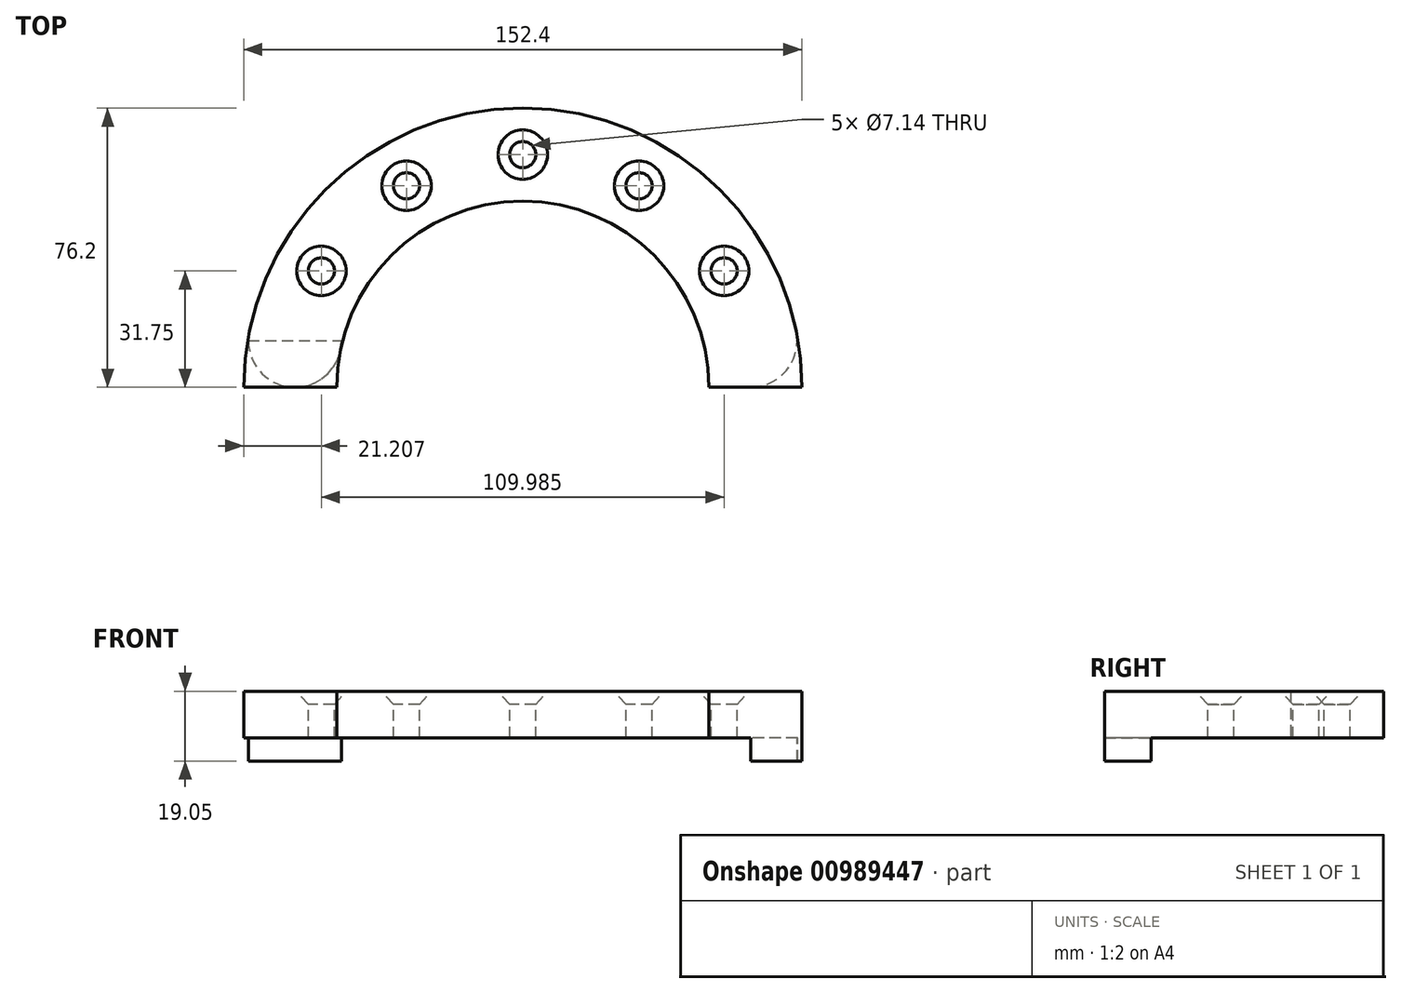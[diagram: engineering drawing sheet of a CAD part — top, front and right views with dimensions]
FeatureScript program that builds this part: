
annotation { "Feature Type Name" : "Feature", "Feature Type Description" : "" }
export const myFeature = defineFeature(function(context is Context, id is Id, definition is map)
    precondition{}
    {
        {
            var Q0;
            Q0=qCreatedBy(makeId("Top.planeOp"),FACE);
            var sketch = newSketch(context, id + "F0", { "sketchPlane" : qUnion([Q0])});
            skArc(sketch, "E0", {"start": v(-50.8, 0) * mm, "mid": v(0, 50.8) * mm, "end": v(50.8, 0) * mm});
            skArc(sketch, "E1", {"start": v(-76.2, 0) * mm, "mid": v(0, 76.2) * mm, "end": v(76.2, 0) * mm});
            skLineSegment(sketch, "E2", {"start": v(-76.2, 0) * mm, "end": v(-50.8, 0) * mm});
            skLineSegment(sketch, "E3", {"start": v(50.8, 0) * mm, "end": v(76.2, 0) * mm});
            skSolve(sketch);
        }
        {
            var Q0;
            Q0 = qSketchRegion(id + "F0", true);
            extrude(context, id + "F1", {"entities" : qUnion([Q0]), "depth" : 12.7 * mm, "offsetDistance" : 25.4 * mm});
        }
        {
            var Q0;
            Q0=makeQuery(id+"F1.opExtrude","CAP_FACE",FACE,{"disambiguationData":[OSD([sQuery(id+"F0.wireOp",EDGE,"E0"),sQuery(id+"F0.wireOp",EDGE,"E1"),sQuery(id+"F0.wireOp",EDGE,"E2"),sQuery(id+"F0.wireOp",EDGE,"E3")])],"isStart":true});
            var sketch = newSketch(context, id + "F2", { "sketchPlane" : qUnion([Q0])});
            skArc(sketch, "E4", {"start": v(-49.52, -12.7) * mm, "mid": v(-62.22, 0) * mm, "end": v(-74.92, -12.7) * mm});
            skLineSegment(sketch, "E5", {"start": v(-75.13, -12.7) * mm, "end": v(-49.52, -12.7) * mm});
            skPoint(sketch, "E6.MirrorCS.end.orphan", {"position": v(-74.92, -12.7) * mm});
            skPoint(sketch, "E6.MirrorCS.start.orphan", {"position": v(-49.52, -12.7) * mm});
            skLineSegment(sketch, "E7", {"start": v(0, 0) * mm, "end": v(0, 11.59) * mm, "construction": true});
            skArc(sketch, "E8.MirrorCS", {"start": v(49.52, -12.7) * mm, "mid": v(62.22, 0) * mm, "end": v(74.92, -12.7) * mm});
            skLineSegment(sketch, "E9.MirrorCS", {"start": v(75.13, -12.7) * mm, "end": v(49.52, -12.7) * mm});
            skPoint(sketch, "E10.MirrorP", {"position": v(49.52, -12.7) * mm});
            skPoint(sketch, "E11.MirrorP", {"position": v(74.92, -12.7) * mm});
            skSolve(sketch);
        }
        {
            var Q0;
            {var subQ0=sQuery(id+"F2.wireOp",EDGE,"E8.MirrorCS");var subQ1=sQuery(id+"F2.wireOp",EDGE,"E9.MirrorCS");var subQ2=makeQuery(id+"F2.imprint","INTERSECT",VERTEX,{"disambiguationData":[OD(0.0)],"derivedFrom":[subQ1,subQ0]});Q0=makeQuery(id+"F2.imprint","IMPRINT",FACE,{"disambiguationData":[TD([[makeQuery(id+"F2.imprint","IMPRINT",EDGE,{"disambiguationData":[TD([[subQ2,1.0]])],"derivedFrom":subQ1}),-1.0]])]});}
            var Q1;
            {var subQ0=sQuery(id+"F2.wireOp",EDGE,"E5");var subQ1=sQuery(id+"F2.wireOp",EDGE,"E4");var subQ2=makeQuery(id+"F2.imprint","INTERSECT",VERTEX,{"disambiguationData":[OD(0.0)],"derivedFrom":[subQ1,subQ0]});Q1=makeQuery(id+"F2.imprint","IMPRINT",FACE,{"disambiguationData":[TD([[makeQuery(id+"F2.imprint","IMPRINT",EDGE,{"disambiguationData":[TD([[subQ2,-1.0]])],"derivedFrom":subQ1}),1.0]])]});}
            extrude(context, id + "F3", {"entities" : qUnion([Q0, Q1]), "operationType" : NewBodyOperationType.ADD, "depth" : 6.35 * mm, "offsetDistance" : 25.4 * mm});
        }
        {
            var Q0;
            Q0=makeQuery(id+"F1.opExtrude","CAP_FACE",FACE,{"disambiguationData":[OSD([sQuery(id+"F0.wireOp",EDGE,"E0"),sQuery(id+"F0.wireOp",EDGE,"E1"),sQuery(id+"F0.wireOp",EDGE,"E2"),sQuery(id+"F0.wireOp",EDGE,"E3")])],"isStart":false});
            var sketch = newSketch(context, id + "F4", { "sketchPlane" : qUnion([Q0])});
            skArc(sketch, "E12", {"start": v(-63.5, 0) * mm, "mid": v(0, 63.5) * mm, "end": v(63.5, 0) * mm, "construction": true});
            skPoint(sketch, "E13", {"position": v(-63.5, 0) * mm});
            skPoint(sketch, "E14.1.0", {"position": v(-55, 31.75) * mm});
            skPoint(sketch, "E14.2.0", {"position": v(-31.75, 55) * mm});
            skPoint(sketch, "E14.3.0", {"position": v(0, 63.5) * mm});
            skPoint(sketch, "E14.4.0", {"position": v(31.75, 55) * mm});
            skPoint(sketch, "E14.5.0", {"position": v(55, 31.75) * mm});
            skPoint(sketch, "E14.6.0", {"position": v(63.5, 0) * mm});
            skLineSegment(sketch, "E14.anchor1", {"start": v(0, 0) * mm, "end": v(-63.5, 0) * mm, "construction": true});
            skLineSegment(sketch, "E14.anchor2", {"start": v(0, 0) * mm, "end": v(63.5, 0) * mm, "construction": true});
            skSolve(sketch);
        }
        {
            var Q0;
            Q0=sQuery(id+"F4.wireOp",VERTEX,"E14.1.0");
            var Q1;
            Q1=sQuery(id+"F4.wireOp",VERTEX,"E14.2.0");
            var Q2;
            Q2=sQuery(id+"F4.wireOp",VERTEX,"E14.3.0");
            var Q3;
            Q3=sQuery(id+"F4.wireOp",VERTEX,"E14.4.0");
            var Q4;
            Q4=sQuery(id+"F4.wireOp",VERTEX,"E14.5.0");
            var Q5;
            Q5=makeQuery(id+"F1.opExtrude","SWEPT_BODY",BODY,{"disambiguationData":[OSD([sQuery(id+"F0.wireOp",EDGE,"E0"),sQuery(id+"F0.wireOp",EDGE,"E1"),sQuery(id+"F0.wireOp",EDGE,"E2"),sQuery(id+"F0.wireOp",EDGE,"E3")])]});
            hole(context, id + "F5", {"style" : HoleStyle.C_SINK, "endStyle" : HoleEndStyle.THROUGH, "standardTappedOrClearance" : lookupTablePath({ "fit" : "Normal (ASME)", "standard" : "ANSI", "size" : "1/4", "type" : "Clearance" }), "standardBlindInLast" : lookupTablePath({ "fit" : "Normal", "standard" : "ANSI", "engagement" : "75%", "pitch" : "20 tpi", "size" : "1/4", "type" : "Clearance & tapped" }), "holeDiameter" : 7.14 * mm, "cSinkDiameter" : 13.5 * mm, "cSinkAngle" : 82 * degree, "majorDiameter" : 6.35 * mm, "isTappedThrough" : true, "tappedDepth" : 12.7 * mm, "tapClearance" : 3, "locations" : qUnion([Q0, Q1, Q2, Q3, Q4]), "scope" : qUnion([Q5])});
        }
    });
